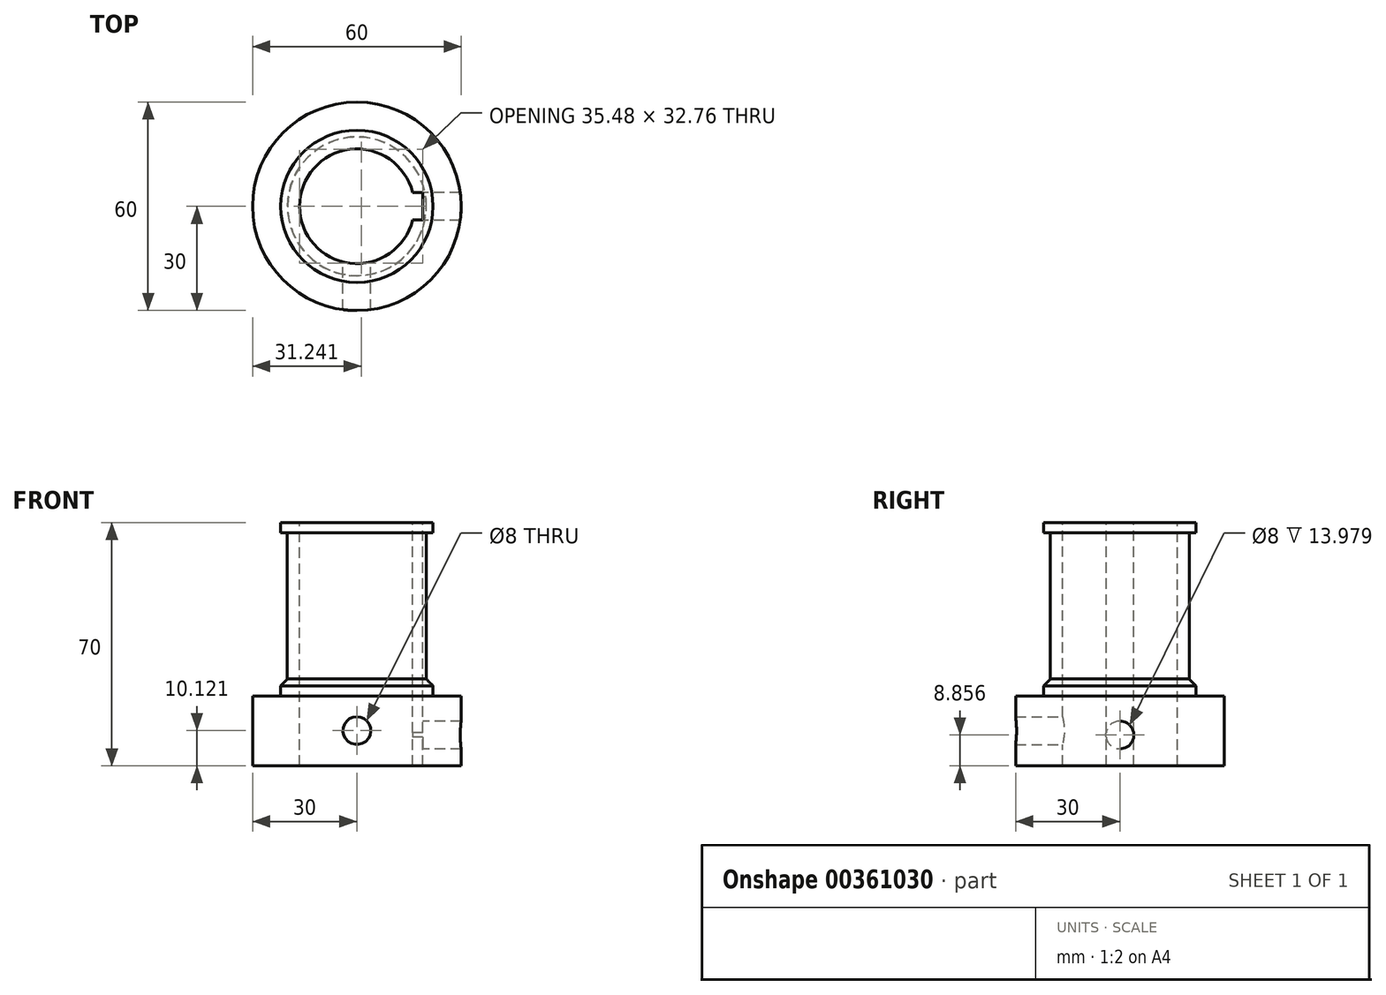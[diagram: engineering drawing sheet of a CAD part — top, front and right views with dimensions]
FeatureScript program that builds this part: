
annotation { "Feature Type Name" : "Feature", "Feature Type Description" : "" }
export const myFeature = defineFeature(function(context is Context, id is Id, definition is map)
    precondition{}
    {
        {
            var Q0;
            Q0=qCreatedBy(makeId("Top.planeOp"),FACE);
            var sketch = newSketch(context, id + "F0", { "sketchPlane" : qUnion([Q0])});
            skCircle(sketch, "E0", {"center": v(0, 0) * mm, "radius": 30 * mm});
            skSolve(sketch);
        }
        {
            var Q0;
            Q0=makeQuery(id+"F0.imprint","IMPRINT",FACE,{"disambiguationData":[TD([[makeQuery(id+"F0.imprint","IMPRINT",EDGE,{"derivedFrom":sQuery(id+"F0.wireOp",EDGE,"E0")}),1.0]])]});
            extrude(context, id + "F1", {"entities" : qUnion([Q0]), "depth" : 20 * mm});
        }
        {
            var Q0;
            Q0=qCreatedBy(makeId("Front.planeOp"),FACE);
            var sketch = newSketch(context, id + "F2", { "sketchPlane" : qUnion([Q0])});
            skCircle(sketch, "E1", {"center": v(0, 10.12) * mm, "radius": 4 * mm});
            skSolve(sketch);
        }
        {
            var Q0;
            Q0 = qSketchRegion(id + "F2", true);
            extrude(context, id + "F3", {"entities" : qUnion([Q0]), "operationType" : NewBodyOperationType.REMOVE, "depth" : 30 * mm});
        }
        {
            var Q0;
            Q0=makeQuery(id+"F1.opExtrude","CAP_FACE",FACE,{"disambiguationData":[OSD([sQuery(id+"F0.wireOp",EDGE,"E0")])],"isStart":false});
            var sketch = newSketch(context, id + "F4", { "sketchPlane" : qUnion([Q0])});
            skCircle(sketch, "E2", {"center": v(0, 0) * mm, "radius": 21.9 * mm});
            skSolve(sketch);
        }
        {
            var Q0;
            Q0=makeQuery(id+"F4.imprint","IMPRINT",FACE,{"disambiguationData":[TD([[makeQuery(id+"F4.imprint","IMPRINT",EDGE,{"derivedFrom":sQuery(id+"F4.wireOp",EDGE,"E2")}),1.0]])]});
            extrude(context, id + "F5", {"entities" : qUnion([Q0]), "operationType" : NewBodyOperationType.ADD, "depth" : 5 * mm});
        }
        {
            var Q0;
            Q0=makeQuery(id+"F5.opExtrude","CAP_EDGE",EDGE,{"disambiguationData":[OSD([sQuery(id+"F4.wireOp",EDGE,"E2")])],"isStart":false});
            chamfer(context, id + "F6", {"entities" : qUnion([Q0]), "width" : 2 * mm, "tangentPropagation" : true});
        }
        {
            var Q0;
            Q0=makeQuery(id+"F5.opExtrude","CAP_FACE",FACE,{"disambiguationData":[OSD([sQuery(id+"F4.wireOp",EDGE,"E2")])],"isStart":false});
            var sketch = newSketch(context, id + "F7", { "sketchPlane" : qUnion([Q0])});
            skCircle(sketch, "E3", {"center": v(0, 0) * mm, "radius": 20 * mm});
            skSolve(sketch);
        }
        {
            var Q0;
            Q0=makeQuery(id+"F7.imprint","IMPRINT",FACE,{"disambiguationData":[TD([[makeQuery(id+"F7.imprint","IMPRINT",EDGE,{"derivedFrom":sQuery(id+"F7.wireOp",EDGE,"E3")}),1.0]])]});
            var Q1;
            {var subQ0=sQuery(id+"F4.wireOp",EDGE,"E2");Q1=makeQuery(id+"F7.imprint","IMPRINT",FACE,{"disambiguationData":[TD([[makeQuery(id+"F7.imprint","IMPRINT",EDGE,{"derivedFrom":makeQuery(id+"F6.opChamfer","BLEND_EDGE",EDGE,{"blendedFrom":[makeQuery(id+"F5.opExtrude","CAP_EDGE",EDGE,{"disambiguationData":[OSD([subQ0])],"isStart":false}),makeQuery(id+"F5.opExtrude","CAP_FACE",FACE,{"disambiguationData":[OSD([subQ0])],"isStart":false})],"blendedInto":[makeQuery(id+"F5.opExtrude","CAP_FACE",FACE,{"disambiguationData":[OSD([subQ0])],"isStart":false})]})}),1.0]])]});}
            extrude(context, id + "F8", {"entities" : qUnion([Q0, Q1]), "operationType" : NewBodyOperationType.ADD, "depth" : 42 * mm});
        }
        {
            var Q0;
            Q0=makeQuery(id+"F8.opExtrude","CAP_FACE",FACE,{"disambiguationData":[OSD([sQuery(id+"F7.wireOp",EDGE,"E3")])],"isStart":false});
            var sketch = newSketch(context, id + "F9", { "sketchPlane" : qUnion([Q0])});
            skCircle(sketch, "E4", {"center": v(0, 0) * mm, "radius": 21.9 * mm});
            skSolve(sketch);
        }
        {
            var Q0;
            Q0=makeQuery(id+"F9.imprint","IMPRINT",FACE,{"disambiguationData":[TD([[makeQuery(id+"F9.imprint","IMPRINT",EDGE,{"derivedFrom":makeQuery(id+"F8.opExtrude","CAP_EDGE",EDGE,{"disambiguationData":[OSD([sQuery(id+"F7.wireOp",EDGE,"E3")])],"isStart":false})}),1.0]])]});
            var Q1;
            Q1=makeQuery(id+"F9.imprint","IMPRINT",FACE,{"disambiguationData":[TD([[makeQuery(id+"F9.imprint","IMPRINT",EDGE,{"derivedFrom":sQuery(id+"F9.wireOp",EDGE,"E4")}),1.0]])]});
            extrude(context, id + "F10", {"entities" : qUnion([Q0, Q1]), "operationType" : NewBodyOperationType.ADD, "depth" : 3 * mm});
        }
        {
            var Q0;
            Q0=makeQuery(id+"F10.opExtrude","CAP_FACE",FACE,{"disambiguationData":[OSD([sQuery(id+"F9.wireOp",EDGE,"E4")])],"isStart":false});
            var sketch = newSketch(context, id + "F11", { "sketchPlane" : qUnion([Q0])});
            skArc(sketch, "E5", {"start": v(16.02, 3.95) * mm, "mid": v(-16.5, 0) * mm, "end": v(16.02, -3.95) * mm});
            skLineSegment(sketch, "E6", {"start": v(16.02, 3.95) * mm, "end": v(18.98, 3.95) * mm});
            skLineSegment(sketch, "E7", {"start": v(16.02, -3.95) * mm, "end": v(18.98, -3.95) * mm});
            skLineSegment(sketch, "E8", {"start": v(18.98, 3.95) * mm, "end": v(18.98, -3.95) * mm});
            skSolve(sketch);
        }
        {
            var Q0;
            Q0=makeQuery(id+"F11.imprint","IMPRINT",FACE,{"disambiguationData":[TD([[makeQuery(id+"F11.imprint","IMPRINT",EDGE,{"derivedFrom":sQuery(id+"F11.wireOp",EDGE,"E5")}),1.0]])]});
            extrude(context, id + "F12", {"entities" : qUnion([Q0]), "operationType" : NewBodyOperationType.REMOVE, "oppositeDirection" : true, "depth" : 70 * mm});
        }
        {
            var Q0;
            Q0=qCreatedBy(makeId("Right.planeOp"),FACE);
            var sketch = newSketch(context, id + "F13", { "sketchPlane" : qUnion([Q0])});
            skCircle(sketch, "E9", {"center": v(0, 8.86) * mm, "radius": 4 * mm});
            skSolve(sketch);
        }
        {
            var Q0;
            Q0 = qSketchRegion(id + "F13", true);
            extrude(context, id + "F14", {"entities" : qUnion([Q0]), "operationType" : NewBodyOperationType.REMOVE, "endBound" : BoundingType.THROUGH_ALL, "depth" : 25 * mm});
        }
    });
